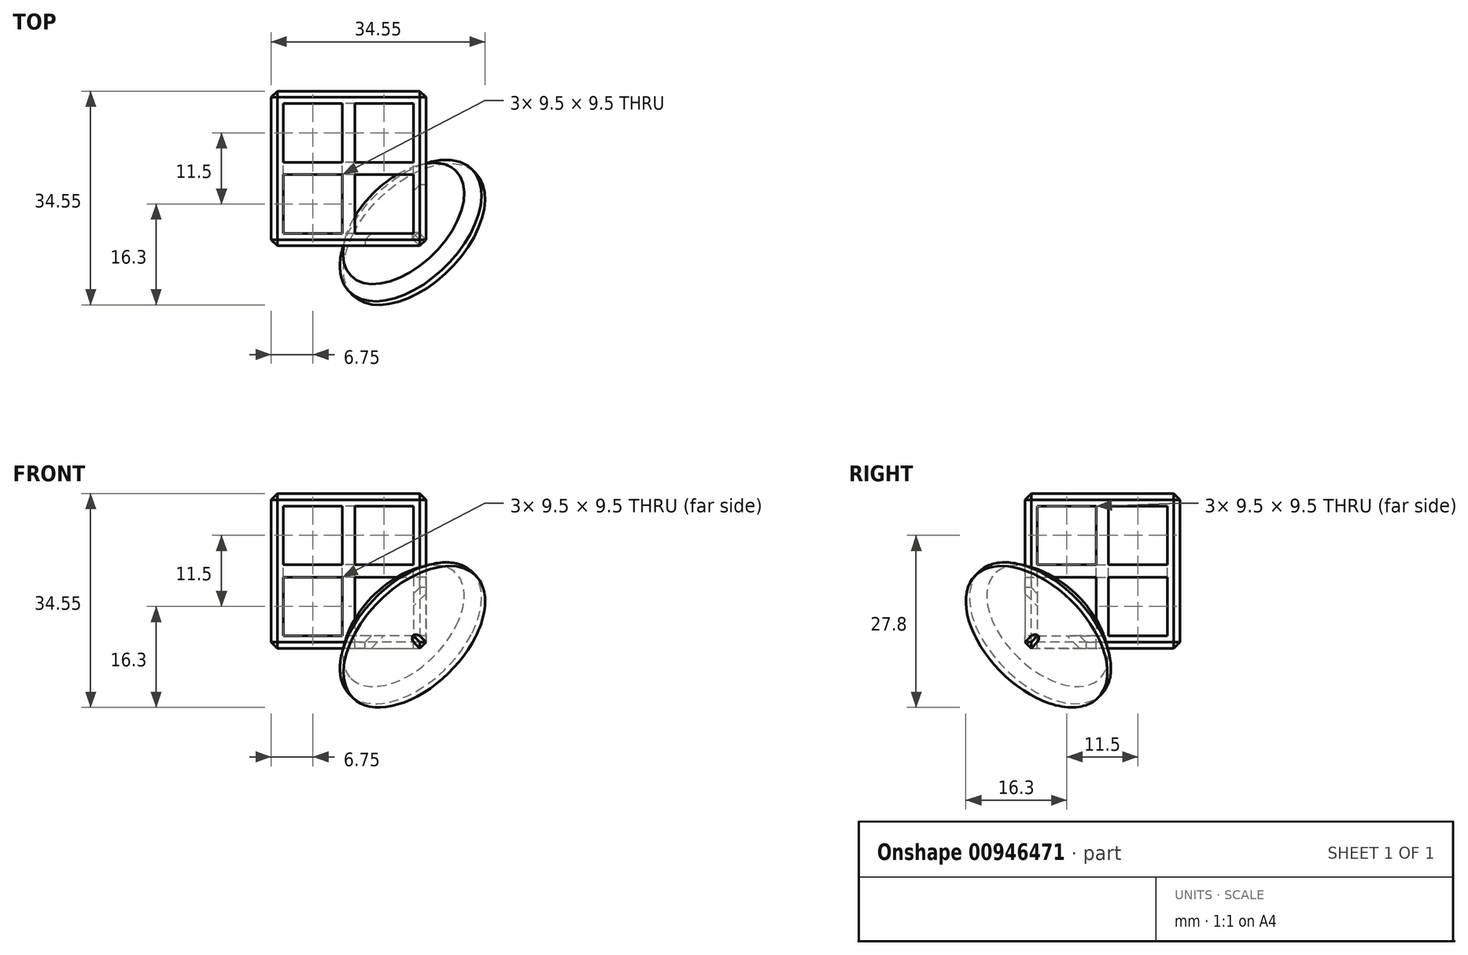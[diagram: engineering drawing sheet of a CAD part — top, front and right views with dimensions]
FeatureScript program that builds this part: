
annotation { "Feature Type Name" : "Feature", "Feature Type Description" : "" }
export const myFeature = defineFeature(function(context is Context, id is Id, definition is map)
    precondition{}
    {
        {
            var Q0;
            Q0=qCreatedBy(makeId("Top.planeOp"),FACE);
            var sketch = newSketch(context, id + "F0", { "sketchPlane" : qUnion([Q0])});
            skLineSegment(sketch, "E0.bottom", {"start": v(12.5, 12.5) * mm, "end": v(-12.5, 12.5) * mm});
            skLineSegment(sketch, "E0.top", {"start": v(12.5, -12.5) * mm, "end": v(-12.5, -12.5) * mm});
            skLineSegment(sketch, "E0.left", {"start": v(12.5, 12.5) * mm, "end": v(12.5, -12.5) * mm});
            skLineSegment(sketch, "E0.right", {"start": v(-12.5, 12.5) * mm, "end": v(-12.5, -12.5) * mm});
            skPoint(sketch, "E0.middle", {"position": v(0, 0) * mm});
            skSolve(sketch);
        }
        {
            var Q0;
            Q0=makeQuery(id+"F0.imprint","IMPRINT",FACE,{"disambiguationData":[TD([[makeQuery(id+"F0.imprint","IMPRINT",EDGE,{"derivedFrom":sQuery(id+"F0.wireOp",EDGE,"E0.bottom")}),1.0]])]});
            extrude(context, id + "F1", {"entities" : qUnion([Q0]), "depth" : 25 * mm, "offsetDistance" : 25 * mm});
        }
        {
            var Q0;
            Q0=makeQuery(id+"F1.opExtrude","SWEPT_FACE",FACE,{"disambiguationData":[OSD([sQuery(id+"F0.wireOp",EDGE,"E0.right")])]});
            var sketch = newSketch(context, id + "F2", { "sketchPlane" : qUnion([Q0])});
            skLineSegment(sketch, "E1.bottom", {"start": v(-12.5, 25) * mm, "end": v(12.5, 25) * mm});
            skLineSegment(sketch, "E1.top", {"start": v(-12.5, 0) * mm, "end": v(12.5, 0) * mm});
            skLineSegment(sketch, "E1.left", {"start": v(-12.5, 25) * mm, "end": v(-12.5, 0) * mm});
            skLineSegment(sketch, "E1.right", {"start": v(12.5, 25) * mm, "end": v(12.5, 0) * mm});
            skLineSegment(sketch, "E2.0", {"start": v(-10.5, 23) * mm, "end": v(10.5, 23) * mm});
            skLineSegment(sketch, "E2.1", {"start": v(-10.5, 23) * mm, "end": v(-10.5, 2) * mm});
            skLineSegment(sketch, "E2.2", {"start": v(-10.5, 2) * mm, "end": v(10.5, 2) * mm});
            skLineSegment(sketch, "E2.3", {"start": v(10.5, 23) * mm, "end": v(10.5, 2) * mm});
            skLineSegment(sketch, "E3", {"start": v(0, 2) * mm, "end": v(0, 23) * mm, "construction": true});
            skLineSegment(sketch, "E4.bottom", {"start": v(1, 23) * mm, "end": v(-1, 23) * mm});
            skLineSegment(sketch, "E4.top", {"start": v(1, 2) * mm, "end": v(-1, 2) * mm});
            skLineSegment(sketch, "E4.left", {"start": v(1, 23) * mm, "end": v(1, 2) * mm});
            skLineSegment(sketch, "E4.right", {"start": v(-1, 23) * mm, "end": v(-1, 2) * mm});
            skPoint(sketch, "E4.middle", {"position": v(0, 12.5) * mm});
            skLineSegment(sketch, "E5.bottom", {"start": v(10.5, 13.5) * mm, "end": v(-10.5, 13.5) * mm});
            skLineSegment(sketch, "E5.top", {"start": v(10.5, 11.5) * mm, "end": v(-10.5, 11.5) * mm});
            skLineSegment(sketch, "E5.left", {"start": v(10.5, 13.5) * mm, "end": v(10.5, 11.5) * mm});
            skLineSegment(sketch, "E5.right", {"start": v(-10.5, 13.5) * mm, "end": v(-10.5, 11.5) * mm});
            skSolve(sketch);
        }
        {
            var Q0;
            {var subQ0=sQuery(id+"F2.wireOp",EDGE,"E2.1");var subQ1=sQuery(id+"F2.wireOp",EDGE,"E2.0");var subQ2=makeQuery(id+"F2.imprint","INTERSECT",VERTEX,{"derivedFrom":[subQ1,subQ0]});Q0=makeQuery(id+"F2.imprint","IMPRINT",FACE,{"disambiguationData":[TD([[makeQuery(id+"F2.imprint","IMPRINT",EDGE,{"disambiguationData":[TD([[subQ2,-1.0]])],"derivedFrom":subQ1}),-1.0]])]});}
            var Q1;
            {var subQ0=sQuery(id+"F2.wireOp",EDGE,"E2.3");var subQ1=sQuery(id+"F2.wireOp",EDGE,"E2.0");var subQ2=makeQuery(id+"F2.imprint","INTERSECT",VERTEX,{"derivedFrom":[subQ1,subQ0]});Q1=makeQuery(id+"F2.imprint","IMPRINT",FACE,{"disambiguationData":[TD([[makeQuery(id+"F2.imprint","IMPRINT",EDGE,{"disambiguationData":[TD([[subQ2,1.0]])],"derivedFrom":subQ1}),-1.0]])]});}
            var Q2;
            {var subQ0=sQuery(id+"F2.wireOp",EDGE,"E2.2");var subQ1=sQuery(id+"F2.wireOp",EDGE,"E2.1");var subQ2=makeQuery(id+"F2.imprint","INTERSECT",VERTEX,{"derivedFrom":[subQ1,subQ0]});Q2=makeQuery(id+"F2.imprint","IMPRINT",FACE,{"disambiguationData":[TD([[makeQuery(id+"F2.imprint","IMPRINT",EDGE,{"disambiguationData":[TD([[subQ2,1.0]])],"derivedFrom":subQ1}),1.0]])]});}
            var Q3;
            {var subQ0=sQuery(id+"F2.wireOp",EDGE,"E2.3");var subQ1=sQuery(id+"F2.wireOp",EDGE,"E2.2");var subQ2=makeQuery(id+"F2.imprint","INTERSECT",VERTEX,{"derivedFrom":[subQ1,subQ0]});Q3=makeQuery(id+"F2.imprint","IMPRINT",FACE,{"disambiguationData":[TD([[makeQuery(id+"F2.imprint","IMPRINT",EDGE,{"disambiguationData":[TD([[subQ2,1.0]])],"derivedFrom":subQ1}),1.0]])]});}
            extrude(context, id + "F3", {"entities" : qUnion([Q0, Q1, Q2, Q3]), "operationType" : NewBodyOperationType.REMOVE, "oppositeDirection" : true, "depth" : 25 * mm, "offsetDistance" : 25 * mm});
        }
        {
            var Q0;
            Q0=makeQuery(id+"F1.opExtrude","SWEPT_FACE",FACE,{"disambiguationData":[OSD([sQuery(id+"F0.wireOp",EDGE,"E0.bottom")])]});
            var sketch = newSketch(context, id + "F4", { "sketchPlane" : qUnion([Q0])});
            skLineSegment(sketch, "E6.bottom", {"start": v(-12.5, 25) * mm, "end": v(12.5, 25) * mm});
            skLineSegment(sketch, "E6.top", {"start": v(-12.5, 0) * mm, "end": v(12.5, 0) * mm});
            skLineSegment(sketch, "E6.left", {"start": v(-12.5, 25) * mm, "end": v(-12.5, 0) * mm});
            skLineSegment(sketch, "E6.right", {"start": v(12.5, 25) * mm, "end": v(12.5, 0) * mm});
            skLineSegment(sketch, "E7.0", {"start": v(10.5, 23) * mm, "end": v(10.5, 2) * mm});
            skLineSegment(sketch, "E7.1", {"start": v(-10.5, 23) * mm, "end": v(10.5, 23) * mm});
            skLineSegment(sketch, "E7.2", {"start": v(-10.5, 23) * mm, "end": v(-10.5, 2) * mm});
            skLineSegment(sketch, "E7.3", {"start": v(-10.5, 2) * mm, "end": v(10.5, 2) * mm});
            skLineSegment(sketch, "E8", {"start": v(0, 0) * mm, "end": v(0, 25) * mm, "construction": true});
            skLineSegment(sketch, "E9.bottom", {"start": v(10.5, 13.5) * mm, "end": v(-10.5, 13.5) * mm});
            skLineSegment(sketch, "E9.top", {"start": v(10.5, 11.5) * mm, "end": v(-10.5, 11.5) * mm});
            skLineSegment(sketch, "E9.left", {"start": v(10.5, 13.5) * mm, "end": v(10.5, 11.5) * mm});
            skLineSegment(sketch, "E9.right", {"start": v(-10.5, 13.5) * mm, "end": v(-10.5, 11.5) * mm});
            skPoint(sketch, "E9.middle", {"position": v(0, 12.5) * mm});
            skLineSegment(sketch, "E10.bottom", {"start": v(1, 23) * mm, "end": v(-1, 23) * mm});
            skLineSegment(sketch, "E10.top", {"start": v(1, 2) * mm, "end": v(-1, 2) * mm});
            skLineSegment(sketch, "E10.left", {"start": v(1, 23) * mm, "end": v(1, 2) * mm});
            skLineSegment(sketch, "E10.right", {"start": v(-1, 23) * mm, "end": v(-1, 2) * mm});
            skSolve(sketch);
        }
        {
            var Q0;
            {var subQ0=sQuery(id+"F4.wireOp",EDGE,"E7.2");var subQ1=sQuery(id+"F4.wireOp",EDGE,"E7.1");var subQ2=makeQuery(id+"F4.imprint","INTERSECT",VERTEX,{"derivedFrom":[subQ1,subQ0]});Q0=makeQuery(id+"F4.imprint","IMPRINT",FACE,{"disambiguationData":[TD([[makeQuery(id+"F4.imprint","IMPRINT",EDGE,{"disambiguationData":[TD([[subQ2,-1.0]])],"derivedFrom":subQ1}),-1.0]])]});}
            var Q1;
            {var subQ0=sQuery(id+"F4.wireOp",EDGE,"E7.1");var subQ1=sQuery(id+"F4.wireOp",EDGE,"E7.0");var subQ2=makeQuery(id+"F4.imprint","INTERSECT",VERTEX,{"derivedFrom":[subQ1,subQ0]});Q1=makeQuery(id+"F4.imprint","IMPRINT",FACE,{"disambiguationData":[TD([[makeQuery(id+"F4.imprint","IMPRINT",EDGE,{"disambiguationData":[TD([[subQ2,-1.0]])],"derivedFrom":subQ1}),-1.0]])]});}
            var Q2;
            {var subQ0=sQuery(id+"F4.wireOp",EDGE,"E7.3");var subQ1=sQuery(id+"F4.wireOp",EDGE,"E7.2");var subQ2=makeQuery(id+"F4.imprint","INTERSECT",VERTEX,{"derivedFrom":[subQ1,subQ0]});Q2=makeQuery(id+"F4.imprint","IMPRINT",FACE,{"disambiguationData":[TD([[makeQuery(id+"F4.imprint","IMPRINT",EDGE,{"disambiguationData":[TD([[subQ2,1.0]])],"derivedFrom":subQ1}),1.0]])]});}
            var Q3;
            {var subQ0=sQuery(id+"F4.wireOp",EDGE,"E7.3");var subQ1=sQuery(id+"F4.wireOp",EDGE,"E7.0");var subQ2=makeQuery(id+"F4.imprint","INTERSECT",VERTEX,{"derivedFrom":[subQ1,subQ0]});Q3=makeQuery(id+"F4.imprint","IMPRINT",FACE,{"disambiguationData":[TD([[makeQuery(id+"F4.imprint","IMPRINT",EDGE,{"disambiguationData":[TD([[subQ2,1.0]])],"derivedFrom":subQ1}),-1.0]])]});}
            extrude(context, id + "F5", {"entities" : qUnion([Q0, Q1, Q2, Q3]), "operationType" : NewBodyOperationType.REMOVE, "oppositeDirection" : true, "depth" : 25 * mm, "offsetDistance" : 25 * mm});
        }
        {
            var Q0;
            Q0=makeQuery(id+"F1.opExtrude","CAP_FACE",FACE,{"disambiguationData":[OSD([sQuery(id+"F0.wireOp",EDGE,"E0.bottom"),sQuery(id+"F0.wireOp",EDGE,"E0.top"),sQuery(id+"F0.wireOp",EDGE,"E0.left"),sQuery(id+"F0.wireOp",EDGE,"E0.right")])],"isStart":false});
            var sketch = newSketch(context, id + "F6", { "sketchPlane" : qUnion([Q0])});
            skLineSegment(sketch, "E11.bottom", {"start": v(-12.5, 12.5) * mm, "end": v(12.5, 12.5) * mm});
            skLineSegment(sketch, "E11.top", {"start": v(-12.5, -12.5) * mm, "end": v(12.5, -12.5) * mm});
            skLineSegment(sketch, "E11.left", {"start": v(-12.5, 12.5) * mm, "end": v(-12.5, -12.5) * mm});
            skLineSegment(sketch, "E11.right", {"start": v(12.5, 12.5) * mm, "end": v(12.5, -12.5) * mm});
            skLineSegment(sketch, "E12.0", {"start": v(-10.5, -10.5) * mm, "end": v(10.5, -10.5) * mm});
            skLineSegment(sketch, "E12.1", {"start": v(-10.5, 10.5) * mm, "end": v(-10.5, -10.5) * mm});
            skLineSegment(sketch, "E12.2", {"start": v(-10.5, 10.5) * mm, "end": v(10.5, 10.5) * mm});
            skLineSegment(sketch, "E12.3", {"start": v(10.5, 10.5) * mm, "end": v(10.5, -10.5) * mm});
            skLineSegment(sketch, "E13", {"start": v(0, -12.5) * mm, "end": v(0, 12.5) * mm, "construction": true});
            skLineSegment(sketch, "E14.bottom", {"start": v(12.5, 1) * mm, "end": v(-12.5, 1) * mm});
            skLineSegment(sketch, "E14.top", {"start": v(12.5, -1) * mm, "end": v(-12.5, -1) * mm});
            skLineSegment(sketch, "E14.left", {"start": v(12.5, 1) * mm, "end": v(12.5, -1) * mm});
            skLineSegment(sketch, "E14.right", {"start": v(-12.5, 1) * mm, "end": v(-12.5, -1) * mm});
            skPoint(sketch, "E14.middle", {"position": v(0, 0) * mm});
            skLineSegment(sketch, "E15.bottom", {"start": v(1, 12.5) * mm, "end": v(-1, 12.5) * mm});
            skLineSegment(sketch, "E15.top", {"start": v(1, -12.5) * mm, "end": v(-1, -12.5) * mm});
            skLineSegment(sketch, "E15.left", {"start": v(1, 12.5) * mm, "end": v(1, -12.5) * mm});
            skLineSegment(sketch, "E15.right", {"start": v(-1, 12.5) * mm, "end": v(-1, -12.5) * mm});
            skSolve(sketch);
        }
        {
            var Q0;
            {var subQ0=sQuery(id+"F6.wireOp",EDGE,"E12.2");var subQ1=sQuery(id+"F6.wireOp",EDGE,"E12.1");var subQ2=makeQuery(id+"F6.imprint","INTERSECT",VERTEX,{"derivedFrom":[subQ1,subQ0]});Q0=makeQuery(id+"F6.imprint","IMPRINT",FACE,{"disambiguationData":[TD([[makeQuery(id+"F6.imprint","IMPRINT",EDGE,{"disambiguationData":[TD([[subQ2,-1.0]])],"derivedFrom":subQ1}),1.0]])]});}
            var Q1;
            {var subQ0=sQuery(id+"F6.wireOp",EDGE,"E12.3");var subQ1=sQuery(id+"F6.wireOp",EDGE,"E12.2");var subQ2=makeQuery(id+"F6.imprint","INTERSECT",VERTEX,{"derivedFrom":[subQ1,subQ0]});Q1=makeQuery(id+"F6.imprint","IMPRINT",FACE,{"disambiguationData":[TD([[makeQuery(id+"F6.imprint","IMPRINT",EDGE,{"disambiguationData":[TD([[subQ2,1.0]])],"derivedFrom":subQ1}),-1.0]])]});}
            var Q2;
            {var subQ0=sQuery(id+"F6.wireOp",EDGE,"E12.3");var subQ1=sQuery(id+"F6.wireOp",EDGE,"E12.0");var subQ2=makeQuery(id+"F6.imprint","INTERSECT",VERTEX,{"derivedFrom":[subQ1,subQ0]});Q2=makeQuery(id+"F6.imprint","IMPRINT",FACE,{"disambiguationData":[TD([[makeQuery(id+"F6.imprint","IMPRINT",EDGE,{"disambiguationData":[TD([[subQ2,1.0]])],"derivedFrom":subQ1}),1.0]])]});}
            var Q3;
            {var subQ0=sQuery(id+"F6.wireOp",EDGE,"E12.1");var subQ1=sQuery(id+"F6.wireOp",EDGE,"E12.0");var subQ2=makeQuery(id+"F6.imprint","INTERSECT",VERTEX,{"derivedFrom":[subQ1,subQ0]});Q3=makeQuery(id+"F6.imprint","IMPRINT",FACE,{"disambiguationData":[TD([[makeQuery(id+"F6.imprint","IMPRINT",EDGE,{"disambiguationData":[TD([[subQ2,-1.0]])],"derivedFrom":subQ1}),1.0]])]});}
            extrude(context, id + "F7", {"entities" : qUnion([Q0, Q1, Q2, Q3]), "operationType" : NewBodyOperationType.REMOVE, "oppositeDirection" : true, "depth" : 25 * mm, "offsetDistance" : 25 * mm});
        }
        {
            var Q0;
            Q0=makeQuery(id+"F1.opExtrude","SWEPT_EDGE",EDGE,{"disambiguationData":[OSD([sQuery(id+"F0.wireOp",EDGE,"E0.bottom"),sQuery(id+"F0.wireOp",EDGE,"E0.left")])]});
            var Q1;
            Q1=makeQuery(id+"F1.opExtrude","CAP_EDGE",EDGE,{"disambiguationData":[OSD([sQuery(id+"F0.wireOp",EDGE,"E0.bottom")])],"isStart":true});
            var Q2;
            Q2=makeQuery(id+"F1.opExtrude","CAP_EDGE",EDGE,{"disambiguationData":[OSD([sQuery(id+"F0.wireOp",EDGE,"E0.left")])],"isStart":true});
            var Q3;
            Q3=makeQuery(id+"F1.opExtrude","CAP_EDGE",EDGE,{"disambiguationData":[OSD([sQuery(id+"F0.wireOp",EDGE,"E0.left")])],"isStart":false});
            var Q4;
            Q4=makeQuery(id+"F1.opExtrude","CAP_EDGE",EDGE,{"disambiguationData":[OSD([sQuery(id+"F0.wireOp",EDGE,"E0.bottom")])],"isStart":false});
            var Q5;
            Q5=makeQuery(id+"F1.opExtrude","CAP_EDGE",EDGE,{"disambiguationData":[OSD([sQuery(id+"F0.wireOp",EDGE,"E0.right")])],"isStart":true});
            var Q6;
            Q6=makeQuery(id+"F1.opExtrude","CAP_EDGE",EDGE,{"disambiguationData":[OSD([sQuery(id+"F0.wireOp",EDGE,"E0.top")])],"isStart":true});
            var Q7;
            Q7=makeQuery(id+"F1.opExtrude","SWEPT_EDGE",EDGE,{"disambiguationData":[OSD([sQuery(id+"F0.wireOp",EDGE,"E0.top"),sQuery(id+"F0.wireOp",EDGE,"E0.left")])]});
            var Q8;
            Q8=makeQuery(id+"F1.opExtrude","CAP_EDGE",EDGE,{"disambiguationData":[OSD([sQuery(id+"F0.wireOp",EDGE,"E0.top")])],"isStart":false});
            var Q9;
            Q9=makeQuery(id+"F1.opExtrude","SWEPT_EDGE",EDGE,{"disambiguationData":[OSD([sQuery(id+"F0.wireOp",EDGE,"E0.top"),sQuery(id+"F0.wireOp",EDGE,"E0.right")])]});
            var Q10;
            Q10=makeQuery(id+"F1.opExtrude","CAP_EDGE",EDGE,{"disambiguationData":[OSD([sQuery(id+"F0.wireOp",EDGE,"E0.right")])],"isStart":false});
            var Q11;
            Q11=makeQuery(id+"F1.opExtrude","SWEPT_EDGE",EDGE,{"disambiguationData":[OSD([sQuery(id+"F0.wireOp",EDGE,"E0.bottom"),sQuery(id+"F0.wireOp",EDGE,"E0.right")])]});
            chamfer(context, id + "F8", {"entities" : qUnion([Q0, Q1, Q2, Q3, Q4, Q5, Q6, Q7, Q8, Q9, Q10, Q11]), "width" : 1 * mm});
        }
        {
            var Q0;
            {var subQ0=sQuery(id+"F0.wireOp",EDGE,"E0.left");var subQ1=sQuery(id+"F0.wireOp",EDGE,"E0.top");Q0=makeQuery(id+"F8.opChamfer","BLEND_FACE",FACE,{"disambiguationData":[OSD([subQ1,subQ0]),TDD([makeQuery(id+"F1.opExtrude","CAP_VERTEX",VERTEX,{"disambiguationData":[OSD([subQ1,subQ0])],"isStart":true})])]});}
            var sketch = newSketch(context, id + "F9", { "sketchPlane" : qUnion([Q0])});
            skLineSegment(sketch, "E16", {"start": v(4.7, 8.84) * mm, "end": v(5.92, 8.84) * mm, "construction": true});
            skLineSegment(sketch, "E17", {"start": v(4.7, 9.55) * mm, "end": v(5.3, 8.49) * mm, "construction": true});
            skCircle(sketch, "E18", {"center": v(5.1, 8.84) * mm, "radius": 10 * mm});
            skSolve(sketch);
        }
        {
            var Q0;
            {var subQ0=sQuery(id+"F0.wireOp",EDGE,"E0.left");var subQ1=sQuery(id+"F0.wireOp",EDGE,"E0.top");var subQ2=makeQuery(id+"F1.opExtrude","CAP_VERTEX",VERTEX,{"disambiguationData":[OSD([subQ1,subQ0])],"isStart":true});Q0=makeQuery(id+"F9.imprint","IMPRINT",FACE,{"disambiguationData":[TD([[makeQuery(id+"F9.imprint","IMPRINT",EDGE,{"derivedFrom":makeQuery(id+"F8.opChamfer","BLEND_EDGE",EDGE,{"blendedFrom":[subQ2,makeQuery(id+"F1.opExtrude","CAP_EDGE",EDGE,{"disambiguationData":[OSD([subQ1])],"isStart":true})],"blendedInto":[]})}),-1.0]])]});}
            var Q1;
            Q1=makeQuery(id+"F9.imprint","IMPRINT",FACE,{"disambiguationData":[TD([[makeQuery(id+"F9.imprint","IMPRINT",EDGE,{"derivedFrom":sQuery(id+"F9.wireOp",EDGE,"E18")}),1.0]])]});
            extrude(context, id + "F10", {"entities" : qUnion([Q0, Q1]), "operationType" : NewBodyOperationType.REMOVE, "oppositeDirection" : true, "depth" : 5.1 * mm, "offsetDistance" : 25 * mm});
        }
        {
            var Q0;
            {var subQ6=sQuery(id+"F0.wireOp",EDGE,"E0.left");var subQ18=sQuery(id+"F0.wireOp",EDGE,"E0.top");Q0=makeQuery(id+"F10.boolean.opBoolean","COPY",FACE,{"disambiguationData":[TD([makeQuery(id+"F8.opChamfer","BLEND_FACE",FACE,{"disambiguationData":[OSD([subQ18,subQ6]),TDD([makeQuery(id+"F1.opExtrude","SWEPT_EDGE",EDGE,{"disambiguationData":[OSD([subQ18,subQ6])]})])]})])],"derivedFrom":makeQuery(id+"F10.opExtrude","CAP_FACE",FACE,{"disambiguationData":[OSD([sQuery(id+"F9.wireOp",EDGE,"E18")])],"isStart":false})});}
            var sketch = newSketch(context, id + "F11", { "sketchPlane" : qUnion([Q0])});
            skCircle(sketch, "E19", {"center": v(5.1, 8.84) * mm, "radius": 3.95 * mm});
            skPoint(sketch, "E19.first.point", {"position": v(7.08, 12.26) * mm});
            skPoint(sketch, "E19.second.point", {"position": v(1.15, 8.84) * mm});
            skPoint(sketch, "E19.third.point", {"position": v(7.08, 5.42) * mm});
            skCircle(sketch, "E20", {"center": v(5.1, 8.84) * mm, "radius": 14 * mm});
            skSolve(sketch);
        }
        {
            var Q0;
            Q0=makeQuery(id+"F11.imprint","IMPRINT",FACE,{"disambiguationData":[TD([[makeQuery(id+"F11.imprint","IMPRINT",EDGE,{"derivedFrom":sQuery(id+"F11.wireOp",EDGE,"E19")}),-1.0]])]});
            var Q1;
            {var subQ0=makeQuery(id+"F10.opExtrude","CAP_FACE",FACE,{"disambiguationData":[OSD([sQuery(id+"F9.wireOp",EDGE,"E18")])],"isStart":false});var subQ1=sQuery(id+"F0.wireOp",EDGE,"E0.left");var subQ2=makeQuery(id+"F1.opExtrude","SWEPT_FACE",FACE,{"disambiguationData":[OSD([subQ1])]});Q1=makeQuery(id+"F11.imprint","IMPRINT",FACE,{"disambiguationData":[TD([[makeQuery(id+"F11.imprint","IMPRINT",EDGE,{"derivedFrom":makeQuery(id+"F10.boolean.opBoolean","INTERSECT",EDGE,{"disambiguationData":[OD(1.0)],"derivedFrom":[subQ2,subQ0]})}),-1.0]])]});}
            var Q2;
            Q2=makeQuery(id+"F11.imprint","IMPRINT",FACE,{"disambiguationData":[TD([[makeQuery(id+"F11.imprint","IMPRINT",EDGE,{"derivedFrom":sQuery(id+"F11.wireOp",EDGE,"E19")}),1.0]])]});
            extrude(context, id + "F12", {"entities" : qUnion([Q0, Q1, Q2]), "operationType" : NewBodyOperationType.ADD, "depth" : 3 * mm, "offsetDistance" : 25 * mm});
        }
        {
            var Q0;
            Q0=makeQuery(id+"F12.opExtrude","CAP_EDGE",EDGE,{"disambiguationData":[OSD([sQuery(id+"F11.wireOp",EDGE,"E20")])],"isStart":true});
            chamfer(context, id + "F13", {"entities" : qUnion([Q0]), "width" : 2 * mm, "tangentPropagation" : true});
        }
    });
